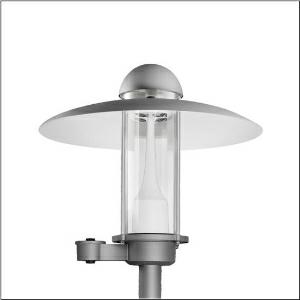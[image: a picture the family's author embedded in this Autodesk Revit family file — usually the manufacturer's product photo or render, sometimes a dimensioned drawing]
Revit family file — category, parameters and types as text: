
# Revit family: city-light_elegance_iq___st1_2a_5xa5265ey14h000022_f597
name_source: partatom
category: Lighting Fixtures
units: mm (PartAtom-declared; Revit-internal decimal feet)

## family parameters
Cut with Voids When Loaded = No
Host = Face
Light Source = No
Part Type = Normal
Room Calculation Point = No
Round Connector Dimension = Use Diameter
Shared = No

## types (1)
- --- (1 x LED, 1460 lm, 10.7 W, 3000K)
    Apparent Load = 11 VA
    CIE Flux Codes = 22 62 94 98 100
    Color Rendering = 70
    Color Temperature = 3000K
    Default Elevation = 1800 mm
    Description = City-Light Elegance iQ, mast luminaire, Module 540 iQ-SR, primary light control with 3 zone facetted reflector, of plastic, silver coated, highly specular, structured, primary optical cover: cover, of PMMA, transparent, light distribution: ST1.2a, light emission: direct distribution, primary light characteristic: asymmetric, installation type: post-top, LED, High Power LED, rated luminous flux: 1.460lm, luminous efficacy: 136lm/W, light colour: 730, colour temperature: 3000K, control gear: iQ-Street Remote, D4i with power reduction, control: optimised constant luminous flux control (CLO 2.0), Desk-Remote (wireless, voltage-free reading and setting of iQ features in the workshop via application-optimized NFC function/RFID function), Light-Fading, Smart-Wire, Night-Set, Lumen-Switch, Temp-Guard, Auto-Match, Street-Remote, pre-setting: logarithmic dimming characteristic, with terminal, 6-pole, max. 2.5mm², mains connection: 230..240V, AC, 50/60Hz, connection cable pre-assembled, cable length: 5,5m, wiring characteristics: H07RN-F, start of lifetime: 11W, end of service life: 11W, reduction: 6W, luminaire housing, upper part, of aluminium, coated, Siteco® metallic grey (DB 702S), diameter: 750mm, height: 675mm, spigot size: d x l = 76 x 70mm (post-top) | with reducer (optional accessory) 60 x 70mm, mounting height: 3..5m, post-top mast mounting element, of diecast aluminium, coated, Siteco® metallic grey (DB 702S), Module 540 iQ-SR, traffic white (RAL 9016), equipment: standard, Smart Interface below and above, protection rating (complete): IP65, insulation class (complete): insulation class II (safety insulation), certification: CE, ENEC, VDE, packaging unit: 1 piece

Light Distribution: ST1.2a
    Height = 675 mm
    Lamp = 1 x LED
    Lamp Light Flux = 1460 lm
    Lamp Power = 10.7 W
    Lamp count = 1
    Length = 750 mm
    Luminous efficacy = 136 lm/W
    Manufacturer = Siteco
    ModVariant = No
    Model = 5XA5265EY14H000022
    Number of Poles = 1
    OnlyDefault = Yes
    Power Factor = 1
    Product Name = City-Light Elegance iQ | ST1.2a
    Product group = mast luminaire | pylon top
    ProductGroupID = 6100
    Protection Class = Protection class II
    Protection Degree = IP 65
    RLX_Detail_Level = 1
    RLX_Emergency_Light_Flux = 0 lm
    RLX_Emergency_Type = 0
    RLX_Emergency_Type_DB = No
    RlxData = <blob elided: 72761 chars, md5=5d2d7417>
    Socket = socket
    Standby Power = 0 W
    System Light Flux = 1460 lm
    System Power = 11 W
    Type Comments = factory setting: luminous flux: 100 % | dim-lin: 254 | 419 mA
    Type Image = l_1005991.jpg
    URL = http://relux.com
    VarID = @adj_086352
    Voltage = 0 V
    Weight = 0.00 kg
    Width = 0 mm  [stored 0 ft]

note: [stored X ft] marks values corroborated as IEEE doubles in the binary element streams (Revit-internal decimal feet)

## geometry (parser evidence)
native form markers: Blend x4, Sweep x10
no freeform markers — native parametric forms only
